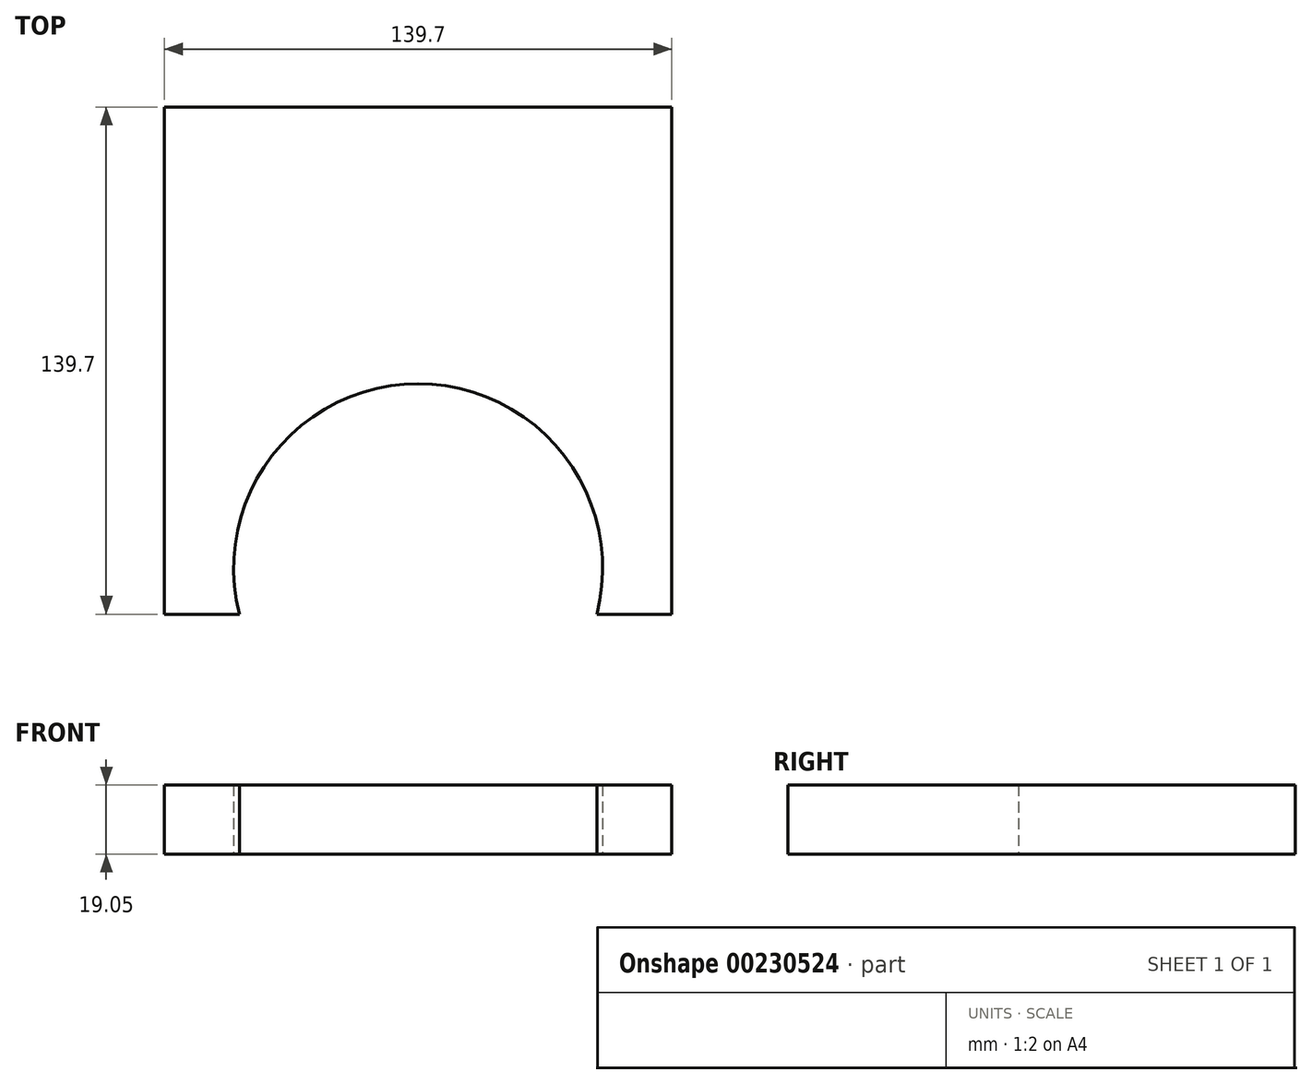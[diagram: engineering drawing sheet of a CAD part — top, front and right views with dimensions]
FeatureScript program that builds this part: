
annotation { "Feature Type Name" : "Feature", "Feature Type Description" : "" }
export const myFeature = defineFeature(function(context is Context, id is Id, definition is map)
    precondition{}
    {
        {
            var Q0;
            Q0=qCreatedBy(makeId("Top.planeOp"),FACE);
            var sketch = newSketch(context, id + "F0", { "sketchPlane" : qUnion([Q0])});
            skLineSegment(sketch, "E0.bottom", {"start": v(-69.85, 69.85) * mm, "end": v(69.85, 69.85) * mm});
            skLineSegment(sketch, "E0.top", {"start": v(-69.85, -69.85) * mm, "end": v(69.85, -69.85) * mm});
            skLineSegment(sketch, "E0.left", {"start": v(-69.85, 69.85) * mm, "end": v(-69.85, -69.85) * mm});
            skLineSegment(sketch, "E0.right", {"start": v(69.85, 69.85) * mm, "end": v(69.85, -69.85) * mm});
            skPoint(sketch, "E0.middle", {"position": v(0, 0) * mm});
            skLineSegment(sketch, "E1", {"start": v(0, -69.85) * mm, "end": v(0, -57.15) * mm});
            skPoint(sketch, "E1.endSnap0", {"position": v(0, -69.85) * mm});
            skArc(sketch, "E2", {"start": v(49.19, -69.85) * mm, "mid": v(0, -6.35) * mm, "end": v(-49.19, -69.85) * mm});
            skSolve(sketch);
        }
        {
            var Q0;
            Q0=makeQuery(id+"F0.imprint","IMPRINT",FACE,{"disambiguationData":[TD([[makeQuery(id+"F0.imprint","IMPRINT",EDGE,{"derivedFrom":sQuery(id+"F0.wireOp",EDGE,"E0.bottom")}),-1.0]])]});
            extrude(context, id + "F1", {"entities" : qUnion([Q0]), "depth" : 19.05 * mm});
        }
    });
